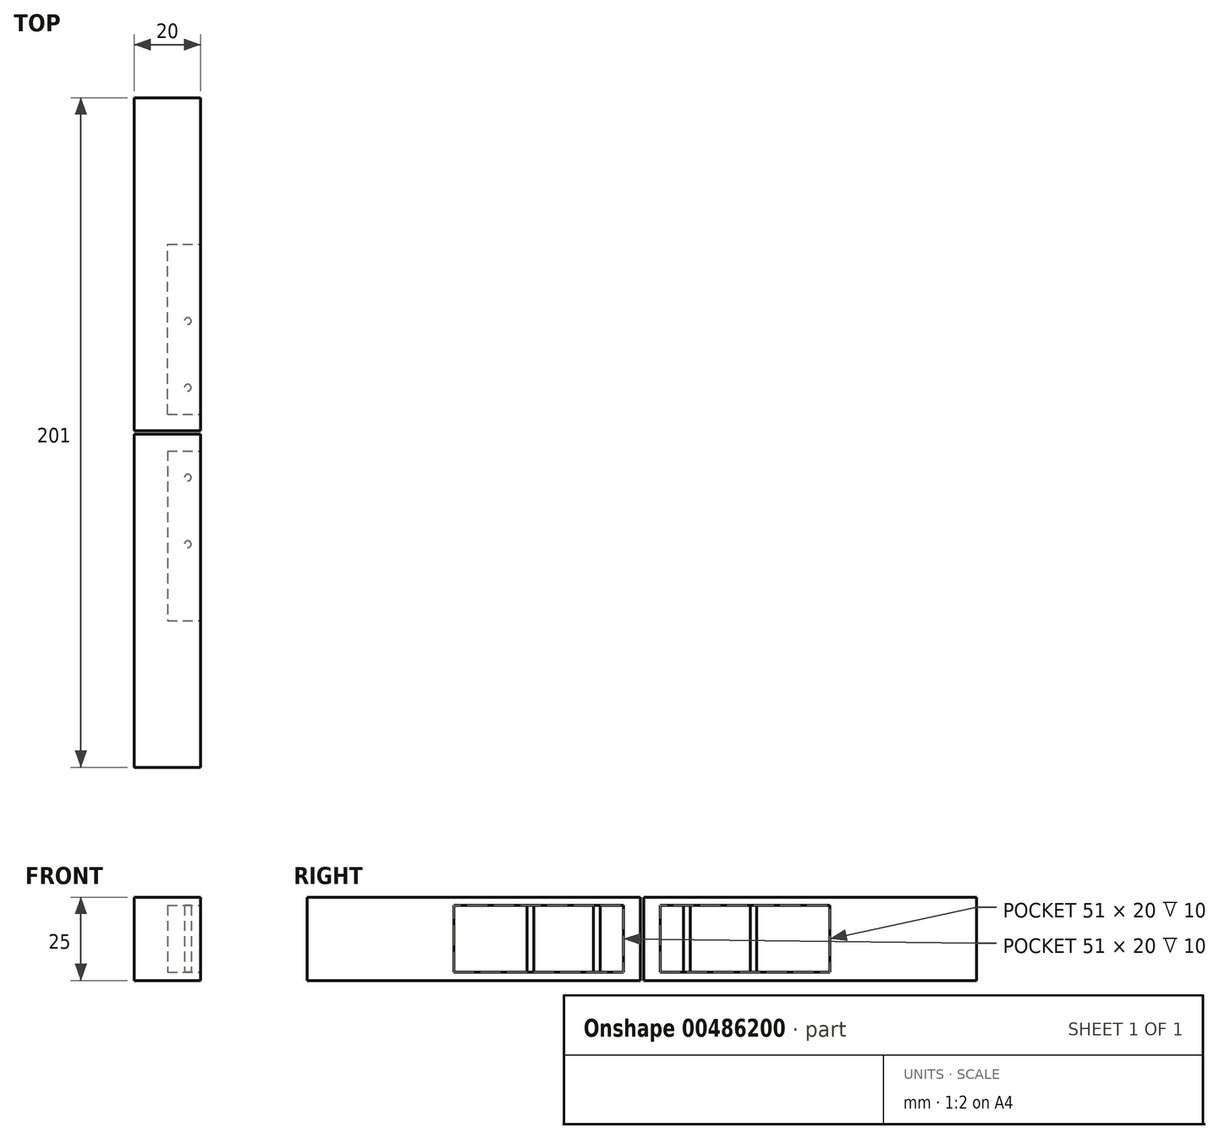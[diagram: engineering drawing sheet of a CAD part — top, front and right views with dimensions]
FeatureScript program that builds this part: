
annotation { "Feature Type Name" : "Feature", "Feature Type Description" : "" }
export const myFeature = defineFeature(function(context is Context, id is Id, definition is map)
    precondition{}
    {
        {
            assignVariable(context, id + "F0", {"name" : "length", "anyValue" : 100 * mm});
        }
        {
            var Q0;
            Q0=qCreatedBy(makeId("Top.planeOp"),FACE);
            var sketch = newSketch(context, id + "F1", { "sketchPlane" : qUnion([Q0])});
            skLineSegment(sketch, "E0.bottom", {"start": v(-44.61, 47.12) * mm, "end": v(-24.61, 47.12) * mm});
            skLineSegment(sketch, "E0.top", {"start": v(-44.61, -52.88) * mm, "end": v(-24.61, -52.88) * mm});
            skLineSegment(sketch, "E0.left", {"start": v(-44.61, 47.12) * mm, "end": v(-44.61, -52.88) * mm});
            skLineSegment(sketch, "E0.right", {"start": v(-24.61, 47.12) * mm, "end": v(-24.61, -52.88) * mm});
            skSolve(sketch);
        }
        {
            var Q0;
            Q0 = qSketchRegion(id + "F1", true);
            extrude(context, id + "F2", {"entities" : qUnion([Q0]), "depth" : 25 * mm});
        }
        {
            var Q0;
            Q0=makeQuery(id+"F2.opExtrude","SWEPT_FACE",FACE,{"disambiguationData":[OSD([sQuery(id+"F1.wireOp",EDGE,"E0.bottom")])]});
            extrude(context, id + "F3", {"entities" : qUnion([Q0]), "depth" : getVariable(context, 'length')});
        }
        {
            var Q0;
            Q0=makeQuery(id+"F2.opExtrude","SWEPT_FACE",FACE,{"disambiguationData":[OSD([sQuery(id+"F1.wireOp",EDGE,"E0.right")])]});
            var sketch = newSketch(context, id + "F4", { "sketchPlane" : qUnion([Q0])});
            skLineSegment(sketch, "E1.bottom", {"start": v(42.12, 22.5) * mm, "end": v(7.12, 22.5) * mm});
            skLineSegment(sketch, "E1.top", {"start": v(42.12, 2.5) * mm, "end": v(7.12, 2.5) * mm});
            skLineSegment(sketch, "E1.left", {"start": v(42.12, 22.5) * mm, "end": v(42.12, 2.5) * mm});
            skLineSegment(sketch, "E1.right", {"start": v(7.12, 22.5) * mm, "end": v(7.12, 2.5) * mm});
            skPoint(sketch, "E2", {"position": v(42.12, 12.5) * mm});
            skPoint(sketch, "E3", {"position": v(47.12, 12.5) * mm});
            skSolve(sketch);
        }
        {
            var Q0;
            Q0=makeQuery(id+"F4.imprint","IMPRINT",FACE,{"disambiguationData":[TD([[makeQuery(id+"F4.imprint","IMPRINT",EDGE,{"derivedFrom":sQuery(id+"F4.wireOp",EDGE,"E1.bottom")}),1.0]])]});
            extrude(context, id + "F5", {"entities" : qUnion([Q0]), "operationType" : NewBodyOperationType.REMOVE, "oppositeDirection" : true, "depth" : 10 * mm});
        }
        {
            var Q0;
            Q0=makeQuery(id+"F5.boolean.opBoolean","COPY",FACE,{"derivedFrom":makeQuery(id+"F5.opExtrude","SWEPT_FACE",FACE,{"disambiguationData":[OSD([sQuery(id+"F4.wireOp",EDGE,"E1.top")])]})});
            var sketch = newSketch(context, id + "F6", { "sketchPlane" : qUnion([Q0])});
            skCircle(sketch, "E4.0", {"center": v(-28.48, 34.12) * mm, "radius": 1.2 * mm, "construction": true});
            skCircle(sketch, "E5", {"center": v(-28.48, 34.12) * mm, "radius": 1 * mm});
            skLineSegment(sketch, "E6", {"start": v(-28.48, 34.12) * mm, "end": v(-28.48, 14.12) * mm, "construction": true});
            skCircle(sketch, "E7", {"center": v(-28.48, 14.12) * mm, "radius": 1 * mm});
            skSolve(sketch);
        }
        {
            var Q0;
            Q0 = qSketchRegion(id + "F6", true);
            var Q1;
            Q1=makeQuery(id+"F5.boolean.opBoolean","COPY",FACE,{"derivedFrom":makeQuery(id+"F5.opExtrude","SWEPT_FACE",FACE,{"disambiguationData":[OSD([sQuery(id+"F4.wireOp",EDGE,"E1.bottom")])]})});
            extrude(context, id + "F7", {"entities" : qUnion([Q0]), "operationType" : NewBodyOperationType.ADD, "endBound" : BoundingType.UP_TO_SURFACE, "endBoundEntityFace" : qUnion([Q1]), "depth" : 25 * mm});
        }
        {
            var Q0;
            Q0=makeQuery(id+"F5.boolean.opBoolean","COPY",FACE,{"derivedFrom":makeQuery(id+"F5.opExtrude","SWEPT_FACE",FACE,{"disambiguationData":[OSD([sQuery(id+"F4.wireOp",EDGE,"E1.right")])]})});
            extrude(context, id + "F8", {"entities" : qUnion([Q0]), "operationType" : NewBodyOperationType.REMOVE, "oppositeDirection" : true, "depth" : 16 * mm});
        }
        {
            var Q0;
            Q0=makeQuery(id+"F3.opExtrude","SWEPT_BODY",BODY,{"disambiguationData":[OSD([sQuery(id+"F1.wireOp",EDGE,"E0.bottom")])]});
            deleteBodies(context, id + "F9", {"entities" : qUnion([Q0])});
        }
        {
            var Q0;
            Q0=makeQuery(id+"F2.opExtrude","SWEPT_FACE",FACE,{"disambiguationData":[OSD([sQuery(id+"F1.wireOp",EDGE,"E0.bottom")])]});
            cPlane(context, id + "F10", {"entities" : qUnion([Q0]), "cplaneType" : CPlaneType.OFFSET, "offset" : .5 * mm, "width" : 150 * mm, "height" : 150 * mm});
        }
        {
            var Q0;
            Q0=makeQuery(id+"F2.opExtrude","SWEPT_BODY",BODY,{"disambiguationData":[OSD([sQuery(id+"F1.wireOp",EDGE,"E0.bottom"),sQuery(id+"F1.wireOp",EDGE,"E0.top"),sQuery(id+"F1.wireOp",EDGE,"E0.left"),sQuery(id+"F1.wireOp",EDGE,"E0.right")])]});
            var Q1;
            Q1=qCreatedBy(id+"F10.planeOp",FACE);
            mirror(context, id + "F11", {"entities" : qUnion([Q0]), "mirrorPlane" : qUnion([Q1])});
        }
    });
